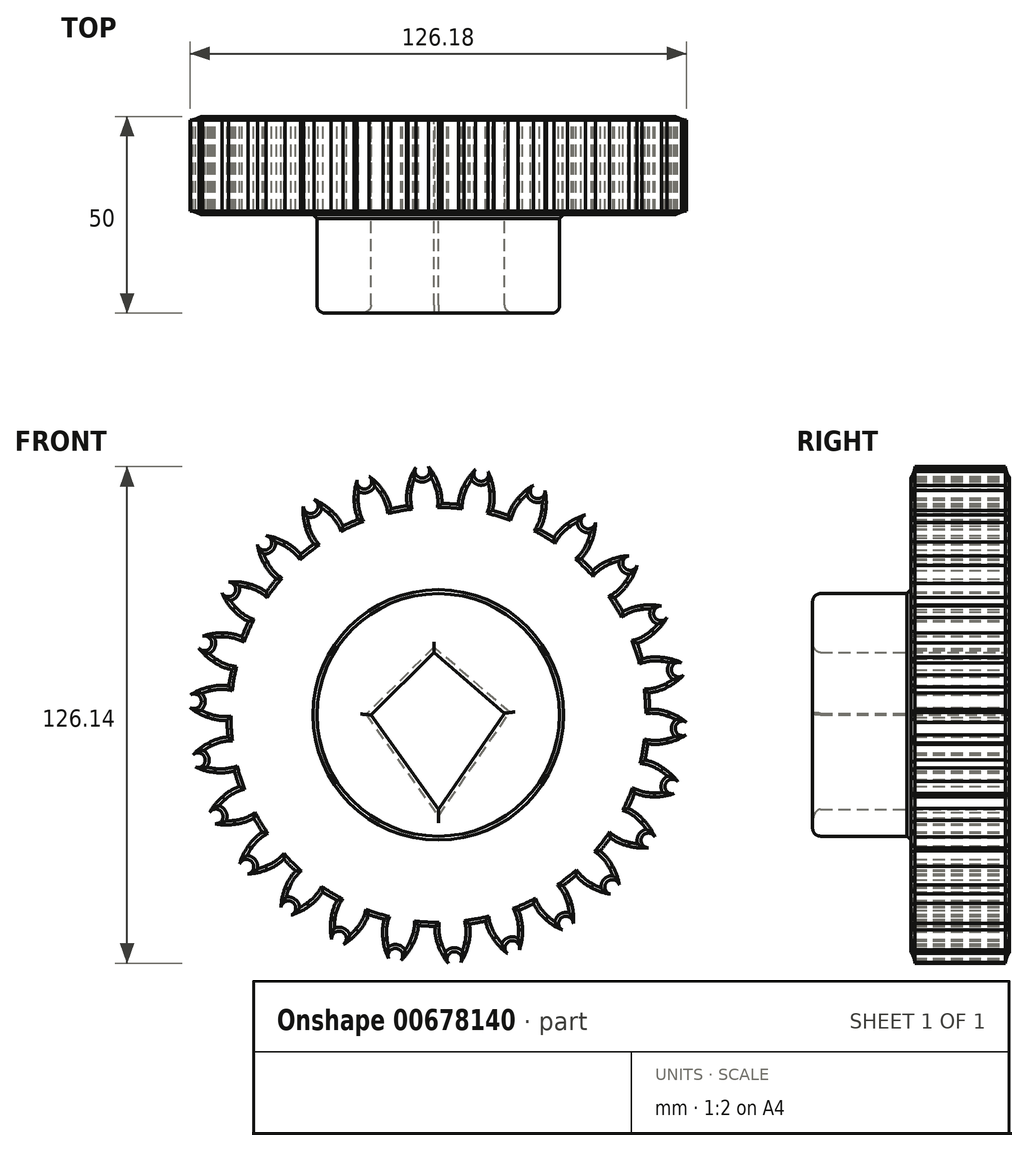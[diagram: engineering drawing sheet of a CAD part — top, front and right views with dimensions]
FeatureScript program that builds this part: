
annotation { "Feature Type Name" : "Feature", "Feature Type Description" : "" }
export const myFeature = defineFeature(function(context is Context, id is Id, definition is map)
    precondition{}
    {
        {
            var Q0;
            Q0=qCreatedBy(makeId("Front.planeOp"),FACE);
            var sketch = newSketch(context, id + "F0", { "sketchPlane" : qUnion([Q0])});
            skCircle(sketch, "E0", {"center": v(0, 0) * mm, "radius": 53.72 * mm});
            skCircle(sketch, "E1", {"center": v(0, 0) * mm, "radius": 58.67 * mm, "construction": true});
            skCircle(sketch, "E2", {"center": v(0, 0) * mm, "radius": 63.5 * mm, "construction": true});
            skLineSegment(sketch, "E3", {"start": v(0, 0) * mm, "end": v(0, 86.26) * mm, "construction": true});
            skLineSegment(sketch, "E4", {"start": v(0, 0) * mm, "end": v(-5.65, 86.26) * mm, "construction": true});
            skLineSegment(sketch, "E5", {"start": v(0, 58.67) * mm, "end": v(-58.15, 58.67) * mm, "construction": true});
            skLineSegment(sketch, "E6", {"start": v(0, 58.67) * mm, "end": v(-58.26, 37.47) * mm, "construction": true});
            skCircle(sketch, "E7", {"center": v(0, 0) * mm, "radius": 55.14 * mm, "construction": true});
            skCircle(sketch, "E8", {"center": v(0, 58.67) * mm, "radius": 14.6 * mm, "construction": true});
            skCircle(sketch, "E9", {"center": v(-13.72, 53.68) * mm, "radius": 14.6 * mm, "construction": true});
            skArc(sketch, "E10", {"start": v(0, 58.67) * mm, "mid": v(-1.18, 61.2) * mm, "end": v(-2.86, 63.44) * mm});
            skArc(sketch, "E11", {"start": v(0.88, 53.71) * mm, "mid": v(0.7, 56.24) * mm, "end": v(0, 58.67) * mm});
            skArc(sketch, "E12.MirrorCS", {"start": v(-7.66, 58.17) * mm, "mid": v(-6.82, 60.83) * mm, "end": v(-5.45, 63.27) * mm});
            skArc(sketch, "E13.MirrorCS", {"start": v(-7.88, 53.14) * mm, "mid": v(-8.04, 55.67) * mm, "end": v(-7.66, 58.17) * mm});
            skArc(sketch, "E14", {"start": v(-5.45, 63.27) * mm, "mid": v(-3.94, 60.17) * mm, "end": v(-2.86, 63.44) * mm});
            skCircle(sketch, "E15", {"center": v(0, 0) * mm, "radius": 30.81 * mm});
            skLineSegment(sketch, "E16", {"start": v(0, -24) * mm, "end": v(-17.1, 0) * mm});
            skLineSegment(sketch, "E17", {"start": v(-17.1, 0) * mm, "end": v(-1.04, 15.85) * mm});
            skLineSegment(sketch, "E18", {"start": v(-1.04, 15.85) * mm, "end": v(16.81, 0.43) * mm});
            skLineSegment(sketch, "E19", {"start": v(16.81, 0.43) * mm, "end": v(0, -24) * mm});
            skSolve(sketch);
        }
        {
            var Q0;
            {var subQ0=sQuery(id+"F0.wireOp",EDGE,"E0");var subQ1=makeQuery(id+"F0.imprint","INTERSECT",VERTEX,{"derivedFrom":[subQ0,sQuery(id+"F0.wireOp",EDGE,"E11")]});Q0=makeQuery(id+"F0.imprint","IMPRINT",FACE,{"disambiguationData":[TD([[makeQuery(id+"F0.imprint","IMPRINT",EDGE,{"disambiguationData":[TD([[subQ1,-1.0]])],"derivedFrom":subQ0}),1.0]])]});}
            var Q1;
            {var subQ0=sQuery(id+"F0.wireOp",EDGE,"E11");Q1=makeQuery(id+"F0.imprint","IMPRINT",FACE,{"disambiguationData":[TD([[makeQuery(id+"F0.imprint","IMPRINT",EDGE,{"derivedFrom":subQ0}),1.0]])]});}
            extrude(context, id + "F1", {"entities" : qUnion([Q0, Q1]), "depth" : 25 * mm, "offsetDistance" : 25 * mm});
        }
        {
            var Q0;
            Q0=makeQuery(id+"F1.opExtrude","SWEPT_BODY",BODY,{"disambiguationData":[OSD([sQuery(id+"F0.wireOp",EDGE,"E0"),sQuery(id+"F0.wireOp",EDGE,"E10"),sQuery(id+"F0.wireOp",EDGE,"E11"),sQuery(id+"F0.wireOp",EDGE,"E12.MirrorCS"),sQuery(id+"F0.wireOp",EDGE,"E13.MirrorCS"),sQuery(id+"F0.wireOp",EDGE,"E14")])]});
            var Q1;
            Q1=makeQuery(id+"F1.opExtrude","SWEPT_FACE",FACE,{"disambiguationData":[OSD([sQuery(id+"F0.wireOp",EDGE,"E0")])]});
            circularPattern(context, id + "F2", {"entities" : qUnion([Q0]), "axis" : qUnion([Q1]), "angle" : 360 * degree, "instanceCount" : 26, "equalSpace" : true});
        }
        {
            var Q0;
            Q0=makeQuery(id+"F0.imprint","IMPRINT",FACE,{"disambiguationData":[TD([[makeQuery(id+"F0.imprint","IMPRINT",EDGE,{"derivedFrom":sQuery(id+"F0.wireOp",EDGE,"E15")}),1.0]])]});
            extrude(context, id + "F3", {"entities" : qUnion([Q0]), "operationType" : NewBodyOperationType.ADD, "depth" : 50 * mm, "offsetDistance" : 25 * mm});
        }
        {
            var Q0;
            {var subQ0=makeQuery(id+"F1.opExtrude","CAP_FACE",FACE,{"disambiguationData":[OSD([sQuery(id+"F0.wireOp",EDGE,"E0"),sQuery(id+"F0.wireOp",EDGE,"E10"),sQuery(id+"F0.wireOp",EDGE,"E11"),sQuery(id+"F0.wireOp",EDGE,"E12.MirrorCS"),sQuery(id+"F0.wireOp",EDGE,"E13.MirrorCS"),sQuery(id+"F0.wireOp",EDGE,"E14"),sQuery(id+"F0.wireOp",EDGE,"E15")])],"isStart":false});Q0=makeQuery(id+"F3.boolean.opBoolean","MERGE",FACE,{"derivedFrom":[subQ0,makeQuery(id+"F2.opPattern","COPY",FACE,{"derivedFrom":subQ0,"instanceName":"1"}),makeQuery(id+"F2.opPattern","COPY",FACE,{"derivedFrom":subQ0,"instanceName":"2"}),makeQuery(id+"F2.opPattern","COPY",FACE,{"derivedFrom":subQ0,"instanceName":"3"}),makeQuery(id+"F2.opPattern","COPY",FACE,{"derivedFrom":subQ0,"instanceName":"4"}),makeQuery(id+"F2.opPattern","COPY",FACE,{"derivedFrom":subQ0,"instanceName":"5"}),makeQuery(id+"F2.opPattern","COPY",FACE,{"derivedFrom":subQ0,"instanceName":"6"}),makeQuery(id+"F2.opPattern","COPY",FACE,{"derivedFrom":subQ0,"instanceName":"7"}),makeQuery(id+"F2.opPattern","COPY",FACE,{"derivedFrom":subQ0,"instanceName":"8"}),makeQuery(id+"F2.opPattern","COPY",FACE,{"derivedFrom":subQ0,"instanceName":"9"}),makeQuery(id+"F2.opPattern","COPY",FACE,{"derivedFrom":subQ0,"instanceName":"10"}),makeQuery(id+"F2.opPattern","COPY",FACE,{"derivedFrom":subQ0,"instanceName":"11"}),makeQuery(id+"F2.opPattern","COPY",FACE,{"derivedFrom":subQ0,"instanceName":"12"}),makeQuery(id+"F2.opPattern","COPY",FACE,{"derivedFrom":subQ0,"instanceName":"13"}),makeQuery(id+"F2.opPattern","COPY",FACE,{"derivedFrom":subQ0,"instanceName":"14"}),makeQuery(id+"F2.opPattern","COPY",FACE,{"derivedFrom":subQ0,"instanceName":"15"}),makeQuery(id+"F2.opPattern","COPY",FACE,{"derivedFrom":subQ0,"instanceName":"16"}),makeQuery(id+"F2.opPattern","COPY",FACE,{"derivedFrom":subQ0,"instanceName":"17"}),makeQuery(id+"F2.opPattern","COPY",FACE,{"derivedFrom":subQ0,"instanceName":"18"}),makeQuery(id+"F2.opPattern","COPY",FACE,{"derivedFrom":subQ0,"instanceName":"19"}),makeQuery(id+"F2.opPattern","COPY",FACE,{"derivedFrom":subQ0,"instanceName":"20"}),makeQuery(id+"F2.opPattern","COPY",FACE,{"derivedFrom":subQ0,"instanceName":"21"}),makeQuery(id+"F2.opPattern","COPY",FACE,{"derivedFrom":subQ0,"instanceName":"22"}),makeQuery(id+"F2.opPattern","COPY",FACE,{"derivedFrom":subQ0,"instanceName":"23"}),makeQuery(id+"F2.opPattern","COPY",FACE,{"derivedFrom":subQ0,"instanceName":"24"}),makeQuery(id+"F2.opPattern","COPY",FACE,{"derivedFrom":subQ0,"instanceName":"25"})]});}
            chamfer(context, id + "F4", {"entities" : qUnion([Q0]), "width" : 1 * mm, "tangentPropagation" : true});
        }
        {
            var Q0;
            {var subQ0=sQuery(id+"F0.wireOp",EDGE,"E15");var subQ1=makeQuery(id+"F1.opExtrude","CAP_FACE",FACE,{"disambiguationData":[OSD([sQuery(id+"F0.wireOp",EDGE,"E0"),sQuery(id+"F0.wireOp",EDGE,"E10"),sQuery(id+"F0.wireOp",EDGE,"E11"),sQuery(id+"F0.wireOp",EDGE,"E12.MirrorCS"),sQuery(id+"F0.wireOp",EDGE,"E13.MirrorCS"),sQuery(id+"F0.wireOp",EDGE,"E14"),subQ0])],"isStart":true});Q0=makeQuery(id+"F3.boolean.opBoolean","MERGE",FACE,{"derivedFrom":[subQ1,makeQuery(id+"F2.opPattern","COPY",FACE,{"derivedFrom":subQ1,"instanceName":"1"}),makeQuery(id+"F2.opPattern","COPY",FACE,{"derivedFrom":subQ1,"instanceName":"2"}),makeQuery(id+"F2.opPattern","COPY",FACE,{"derivedFrom":subQ1,"instanceName":"3"}),makeQuery(id+"F2.opPattern","COPY",FACE,{"derivedFrom":subQ1,"instanceName":"4"}),makeQuery(id+"F2.opPattern","COPY",FACE,{"derivedFrom":subQ1,"instanceName":"5"}),makeQuery(id+"F2.opPattern","COPY",FACE,{"derivedFrom":subQ1,"instanceName":"6"}),makeQuery(id+"F2.opPattern","COPY",FACE,{"derivedFrom":subQ1,"instanceName":"7"}),makeQuery(id+"F2.opPattern","COPY",FACE,{"derivedFrom":subQ1,"instanceName":"8"}),makeQuery(id+"F2.opPattern","COPY",FACE,{"derivedFrom":subQ1,"instanceName":"9"}),makeQuery(id+"F2.opPattern","COPY",FACE,{"derivedFrom":subQ1,"instanceName":"10"}),makeQuery(id+"F2.opPattern","COPY",FACE,{"derivedFrom":subQ1,"instanceName":"11"}),makeQuery(id+"F2.opPattern","COPY",FACE,{"derivedFrom":subQ1,"instanceName":"12"}),makeQuery(id+"F2.opPattern","COPY",FACE,{"derivedFrom":subQ1,"instanceName":"13"}),makeQuery(id+"F2.opPattern","COPY",FACE,{"derivedFrom":subQ1,"instanceName":"14"}),makeQuery(id+"F2.opPattern","COPY",FACE,{"derivedFrom":subQ1,"instanceName":"15"}),makeQuery(id+"F2.opPattern","COPY",FACE,{"derivedFrom":subQ1,"instanceName":"16"}),makeQuery(id+"F2.opPattern","COPY",FACE,{"derivedFrom":subQ1,"instanceName":"17"}),makeQuery(id+"F2.opPattern","COPY",FACE,{"derivedFrom":subQ1,"instanceName":"18"}),makeQuery(id+"F2.opPattern","COPY",FACE,{"derivedFrom":subQ1,"instanceName":"19"}),makeQuery(id+"F2.opPattern","COPY",FACE,{"derivedFrom":subQ1,"instanceName":"20"}),makeQuery(id+"F2.opPattern","COPY",FACE,{"derivedFrom":subQ1,"instanceName":"21"}),makeQuery(id+"F2.opPattern","COPY",FACE,{"derivedFrom":subQ1,"instanceName":"22"}),makeQuery(id+"F2.opPattern","COPY",FACE,{"derivedFrom":subQ1,"instanceName":"23"}),makeQuery(id+"F2.opPattern","COPY",FACE,{"derivedFrom":subQ1,"instanceName":"24"}),makeQuery(id+"F2.opPattern","COPY",FACE,{"derivedFrom":subQ1,"instanceName":"25"}),makeQuery(id+"F3.opExtrude","CAP_FACE",FACE,{"disambiguationData":[OSD([subQ0,sQuery(id+"F0.wireOp",EDGE,"E16"),sQuery(id+"F0.wireOp",EDGE,"E17"),sQuery(id+"F0.wireOp",EDGE,"E18"),sQuery(id+"F0.wireOp",EDGE,"E19")])],"isStart":true})]});}
            chamfer(context, id + "F5", {"entities" : qUnion([Q0]), "width" : 1 * mm, "tangentPropagation" : true});
        }
        {
            var Q0;
            Q0=makeQuery(id+"F3.opExtrude","CAP_FACE",FACE,{"disambiguationData":[OSD([sQuery(id+"F0.wireOp",EDGE,"E15"),sQuery(id+"F0.wireOp",EDGE,"E16"),sQuery(id+"F0.wireOp",EDGE,"E17"),sQuery(id+"F0.wireOp",EDGE,"E18"),sQuery(id+"F0.wireOp",EDGE,"E19")])],"isStart":false});
            fillet(context, id + "F6", {"entities" : qUnion([Q0]), "radius" : 2 * mm, "tangentPropagation" : true, "allowEdgeOverflow" : false});
        }
    });
